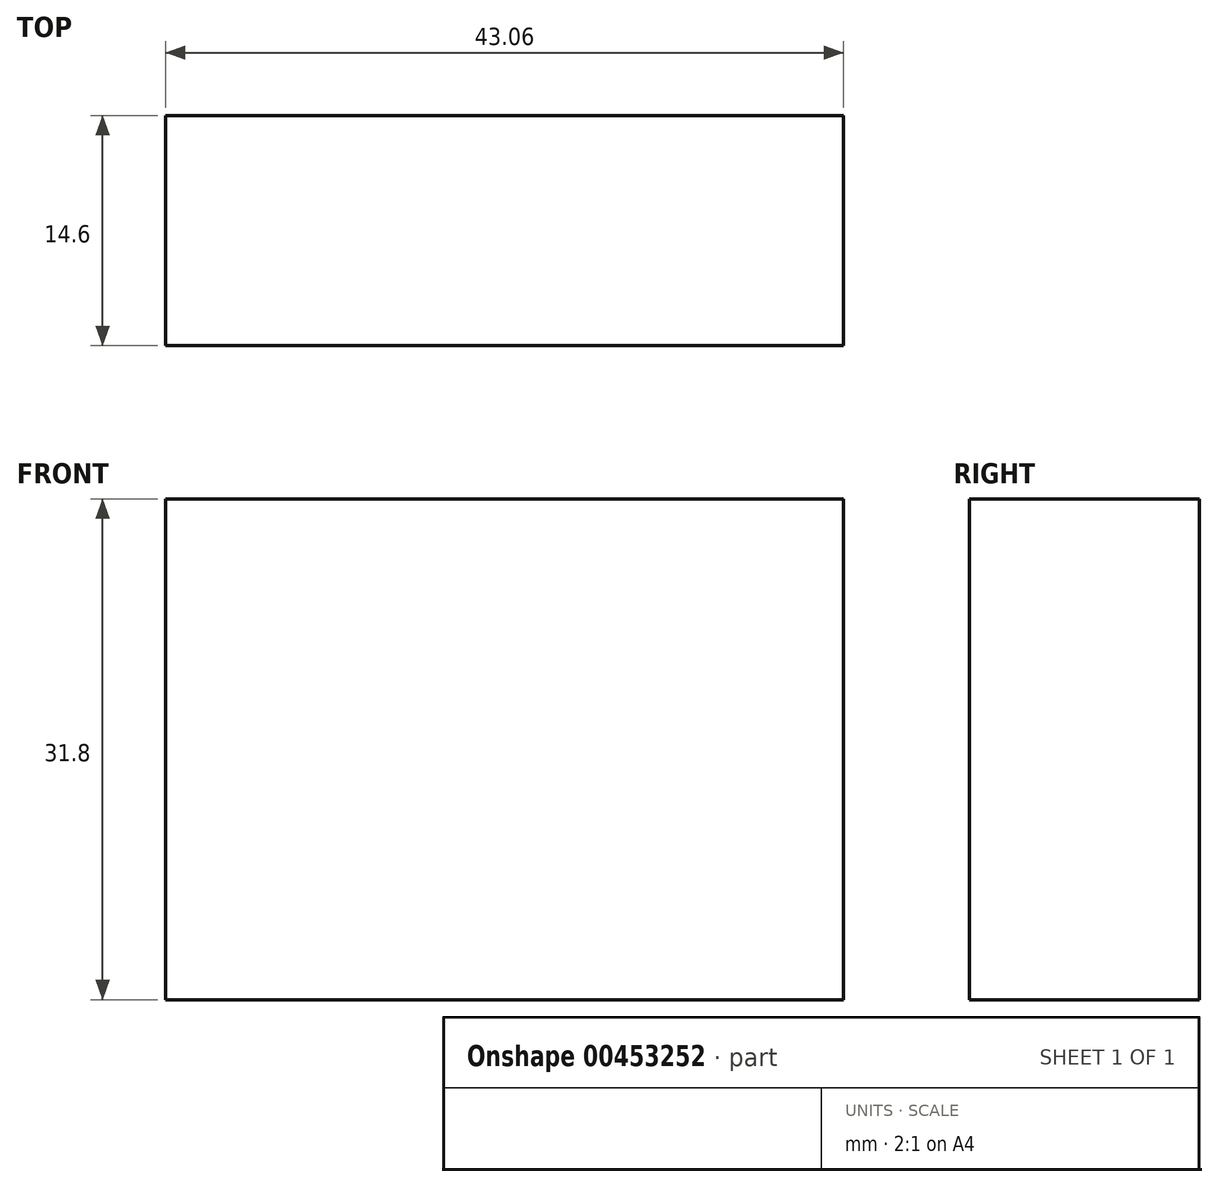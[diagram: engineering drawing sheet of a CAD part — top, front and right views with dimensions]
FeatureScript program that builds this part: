
annotation { "Feature Type Name" : "Feature", "Feature Type Description" : "" }
export const myFeature = defineFeature(function(context is Context, id is Id, definition is map)
    precondition{}
    {
        {
            var Q0;
            Q0=qCreatedBy(makeId("Front.planeOp"),FACE);
            var sketch = newSketch(context, id + "F0", { "sketchPlane" : qUnion([Q0])});
            skLineSegment(sketch, "E0.bottom", {"start": v(-23.4, 6.64) * mm, "end": v(19.66, 6.64) * mm});
            skLineSegment(sketch, "E0.top", {"start": v(-23.4, -25.16) * mm, "end": v(19.66, -25.16) * mm});
            skLineSegment(sketch, "E0.left", {"start": v(-23.4, 6.64) * mm, "end": v(-23.4, -25.16) * mm});
            skLineSegment(sketch, "E0.right", {"start": v(19.66, 6.64) * mm, "end": v(19.66, -25.16) * mm});
            skSolve(sketch);
        }
        {
            var Q0;
            Q0 = qSketchRegion(id + "F0", true);
            extrude(context, id + "F1", {"entities" : qUnion([Q0]), "depth" : 14.6 * mm});
        }
    });
